# Revit family: Electrical_Equipment-Poke_Through-Hubbell_Wiring-System_One-S1R10
name_source: partatom
category: Electrical Fixtures
revit_build: Autodesk Revit Architecture 2015 (Build: 20140606_1530(x64)
units: mm (PartAtom-declared; Revit-internal decimal feet)

## types (1)
- S1R10PTFIT
    Assembly Code = D5020115
    BIMobject category = Distribution
    BIMobject category code = electrical-distribution
    BIMobject main category = Electrical
    BIMobject main category code = electrical
    Brand url = http://www.hubbell-wiring.com
    Cover Material = Metal-Hubbell-Aluminum
    Default Elevation = 0' - 0"
    Description = System One - 10" Poke Through
    Design country = United States
    Edition number = 1
    Electrical Connector Description = Power Connector
    Hardware Material = Metal-Hubbell-Steel
    IFC Classification = Electric Distribution
    Load Classification = Power
    Manufacturer = Hubbell Wiring Device-Kellems
    Manufacturer country = United States
    Manufacturer name = Hubbell Wiring Device-Kellems
    Masterformat 2014 Code = 26 05 33.16
    Masterformat 2014 Description = Boxes for Electrical Systems
    Material main = Aluminium
    Model = S1R10PTFIT
    NBS Reference Code = 70
    NBS Reference Description = Electrical Elements
    Nominal height = 0' - 0"
    Nominal width = 0' - 0"
    Number of Poles = 1
    OmniClass Code = 23-35 33 15
    OmniClass Description = Electrical Junction Boxes
    Power Factor = 1
    Product Documentation Link = https://www.hubbell.com
    Product Guid = c33ab74c-d66d-4844-93a8-ddf9fadcabf6
    Product Page URL = https://www.hubbell.com
    Product SKU = systemone-s1r10
    Product data url = https://bimobject.com
    Product family = Raceway and Boxes for Electrical Systems
    Product group = SystemOne Recessed
    Product url = https://www.hubbell.com
    QR code = http://bimobject.com
    UNSPSC Code = 39121303
    URL = http://www.hubbell-wiring.com
    Uniclass 1.4 Code = L7466
    Uniclass 1.4 Description = Junction boxes, terminal boxes
    Uniclass 2.0 Code = EE-70
    Uniclass 2.0 Description = Electrical Elements
    Voltage = 120 V
    Weight Net (Kg) = 0

## geometry (parser evidence)
native form markers: Blend x6, Sweep x12
no freeform markers — native parametric forms only
